# Revit family: IS_Eurovit_V9210_BIM_DE
name_source: partatom
category: Plumbing Fixtures
revit_build: Autodesk Revit MEP 2016 (Build: 20161004_0715(x64)
units: mm (PartAtom-declared; Revit-internal decimal feet)

## family parameters
Always vertical = No
Cut with Voids When Loaded = No
OmniClass Number = 23.45.05.14.14
OmniClass Title = Sinks/Lavatories
Part Type = Normal
Room Calculation Point = No
Round Connector Dimension = Use Diameter
Shared = No
Work Plane-Based = No

## types (1)
- V921001 - EUROVIT semi pedestal
    Accessories = www.idealstandard.de\ersatzteile
    AssetType = Fixed
    BIMObjectName = ISI_IdealStandard_Legs,Pedestals,HangersAndStringers_Eurovit_V921001
    BIMobject category = Basins
    BOSUseNativeGeometries = 1
    BarCode = 8595095971189
    Brand = Ideal Standard
    Brand url = http://www.idealstandard.de
    CodePerformance = 0
    Color = White
    ConnectionType = Plumbing
    Cost = 0 $
    CurrencyUnit = €
    CurrentRevision = 1
    Date of publishing = 20/12/2017
    Description = IS Wandsäule EUROVIT für Waschtisch Weiß
    DrainSize = 0 mm  [stored 0 ft]
    DurationUnit = Year
    EAN code = https://8595095971189
    Edition number = 1
    ExpectedLife = 25
    Features = IS Wandsäule EUROVIT für Waschtisch Weiß
    Finish = White
    IFC Classification = Sanitary Terminal
    IfcExportAs = IfcSanitaryTerminalType
    Installation instructions = http://www.idealstandard.de
    InstallationInstructions = www.idealstandard.de\produkte
    MainColor = White
    MaintenanceInformation = www.idealstandard.de\produkte
    Manufacturer name = Ideal Standard
    ManufacturerURL = http://www.idealstandard.de
    Material = Vitreous china
    Material main = Ceramics
    Model = V921001
    ModelNumber = V921001
    ModelReference = IS Wandsäule EUROVIT für Waschtisch Weiß
    NBS Reference Code = 85-45
    NBS Reference Description = Legs, Pedestals, Grids And Hangers
    Name = Legs,Pedestals,HangersAndStringers_Eurovit_V921001
    NettWeight = 6.57 Kg
    Nominal height = 0
    Nominal width = 0
    NominalDepth = 299 mm  [stored 0.980971 ft]
    NominalHeight = 370 mm
    NominalLength = 299 mm  [stored 0.980971 ft]
    NominalWidth = 250 mm
    OmniClass Code = 23-21 25 23 15
    OmniClass Description = Pedestals
    Product Guid = d977c7d9-84d9-4882-b558-78206598dfa2
    Product SKU = V9210
    Product data url = https://bimobject.com
    Product family = Sanitary
    Product group = Pedestal
    Product name = EUROVIT semi pedestal
    Product url = http://www.idealstandard.de
    ProductInformation = www.idealstandard.de/produkte
    QR code = http://bimobject.com
    Shape = Sculptured
    Size = 370 x 299 x 250mm
    Space = Internal
    SpareParts = www.idealstandard.de/ersatzteile
    Technical description = http://www.idealstandard.de
    URL = http://www.idealstandard.de
    Uniclass 1.4 Code = L7212
    Uniclass 1.4 Description = Washbasins
    Uniclass 2.0 Code = PR-85-45
    Uniclass 2.0 Description = Legs, Pedestals, Grids And Hangers
    Uniclass 2015 Code = Pr_20_85_47
    Uniclass 2015 Name = Legs, pedestals, hangers and stringers
    Uniclass2015Code = Pr_20_85_47
    Uniclass2015Title = Legs, pedestals, hangers and stringers
    Uniclass2015Version = Products v1.1
    Version = 1
    VolumeUnits = Litres
    Weight Net (Kg) = 6.57

note: [stored X ft] marks values corroborated as IEEE doubles in the binary element streams (Revit-internal decimal feet)

## geometry (parser evidence)
native form markers: Blend x4, Sweep x1
no freeform markers — native parametric forms only
